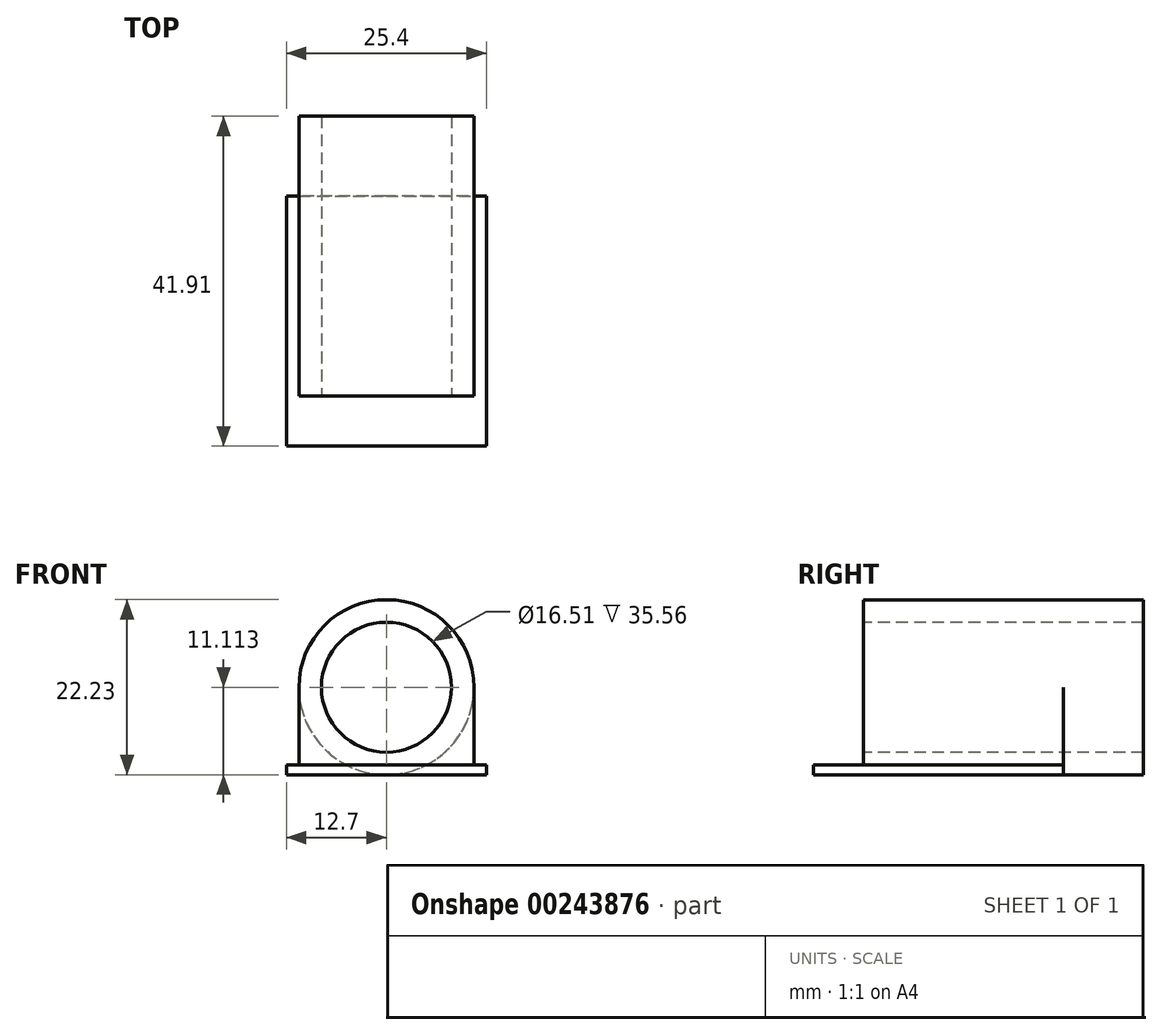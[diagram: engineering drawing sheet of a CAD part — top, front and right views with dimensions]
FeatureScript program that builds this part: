
annotation { "Feature Type Name" : "Feature", "Feature Type Description" : "" }
export const myFeature = defineFeature(function(context is Context, id is Id, definition is map)
    precondition{}
    {
        {
            var Q0;
            Q0=qCreatedBy(makeId("Top.planeOp"),FACE);
            var sketch = newSketch(context, id + "F0", { "sketchPlane" : qUnion([Q0])});
            skCircle(sketch, "E0", {"center": v(0, 0) * mm, "radius": 11.11 * mm});
            skSolve(sketch);
        }
        {
            var Q0;
            Q0=qSketchRegion(id+"F0",true);
            extrude(context, id + "F1", {"entities" : qUnion([Q0]), "depth" : 10.16 * mm, "hasSecondDirection" : true, "secondDirectionOppositeDirection" : true, "secondDirectionDepth" : 25.4 * mm});
        }
        {
            var Q0;
            Q0=makeQuery(id+"F1.opExtrude","CAP_FACE",FACE,{"disambiguationData":[OSD([sQuery(id+"F0.wireOp",EDGE,"E0")])],"isStart":false});
            var sketch = newSketch(context, id + "F2", { "sketchPlane" : qUnion([Q0])});
            skLineSegment(sketch, "E1.bottom", {"start": v(12.7, -11.11) * mm, "end": v(-12.7, -11.11) * mm});
            skLineSegment(sketch, "E1.top", {"start": v(12.7, -9.84) * mm, "end": v(-12.7, -9.84) * mm});
            skLineSegment(sketch, "E1.left", {"start": v(12.7, -11.11) * mm, "end": v(12.7, -9.84) * mm});
            skLineSegment(sketch, "E1.right", {"start": v(-12.7, -11.11) * mm, "end": v(-12.7, -9.84) * mm});
            skPoint(sketch, "E1.middle", {"position": v(0, -10.48) * mm});
            skSolve(sketch);
        }
        {
            var Q0;
            Q0=qSketchRegion(id+"F2",true);
            extrude(context, id + "F3", {"entities" : qUnion([Q0]), "operationType" : NewBodyOperationType.ADD, "depth" : 6.35 * mm, "hasSecondDirection" : true, "secondDirectionOppositeDirection" : true, "secondDirectionDepth" : 25.4 * mm});
        }
        {
            var Q0;
            Q0=qCreatedBy(makeId("Top.planeOp"),FACE);
            cPlane(context, id + "F4", {"entities" : qUnion([Q0]), "cplaneType" : CPlaneType.OFFSET, "offset" : 10.16 * mm, "width" : 152.4 * mm, "height" : 152.4 * mm});
        }
        {
            var Q0;
            Q0=qCreatedBy(id+"F4.planeOp",FACE);
            var sketch = newSketch(context, id + "F5", { "sketchPlane" : qUnion([Q0])});
            skArc(sketch, "E2", {"start": v(11.11, 0) * mm, "mid": v(0, 11.11) * mm, "end": v(-11.11, 0) * mm});
            skLineSegment(sketch, "E3", {"start": v(-11.11, 0) * mm, "end": v(-11.11, -10.67) * mm});
            skLineSegment(sketch, "E4", {"start": v(11.11, 0) * mm, "end": v(11.11, -10.67) * mm});
            skLineSegment(sketch, "E5", {"start": v(-11.11, -10.67) * mm, "end": v(11.11, -10.67) * mm});
            skSolve(sketch);
        }
        {
            var Q0;
            Q0=qSketchRegion(id+"F5",true);
            extrude(context, id + "F6", {"entities" : qUnion([Q0]), "operationType" : NewBodyOperationType.ADD, "oppositeDirection" : true, "depth" : 25.4 * mm});
        }
        {
            var Q0;
            Q0=makeQuery(id+"F1.opExtrude","CAP_FACE",FACE,{"disambiguationData":[OSD([sQuery(id+"F0.wireOp",EDGE,"E0")])],"isStart":false});
            var sketch = newSketch(context, id + "F7", { "sketchPlane" : qUnion([Q0])});
            skCircle(sketch, "E6", {"center": v(0, 0) * mm, "radius": 8.26 * mm});
            skSolve(sketch);
        }
        {
            var Q0;
            Q0=qSketchRegion(id+"F7",true);
            extrude(context, id + "F8", {"entities" : qUnion([Q0]), "operationType" : NewBodyOperationType.REMOVE, "endBound" : BoundingType.THROUGH_ALL, "oppositeDirection" : true, "depth" : 25.4 * mm});
        }
        {
            var Q0;
            Q0=makeQuery(id+"F1.opExtrude","SWEPT_BODY",BODY,{"disambiguationData":[OSD([sQuery(id+"F0.wireOp",EDGE,"E0")])]});
            var Q1;
            {var subQ0=sQuery(id+"F2.wireOp",EDGE,"E1.bottom");var subQ1=sQuery(id+"F2.wireOp",EDGE,"E1.right");Q1=makeQuery(id+"F3.boolean.opBoolean","SPLIT",EDGE,{"disambiguationData":[TD([makeQuery(id+"F3.opExtrude","SWEPT_FACE",FACE,{"disambiguationData":[OSD([subQ1])]})])],"derivedFrom":makeQuery(id+"F3.opExtrude","CAP_EDGE",EDGE,{"disambiguationData":[OSD([subQ0])],"isStart":true})});}
            transform(context, id + "F9", {"entities" : qUnion([Q0]), "transformType" : TransformType.ROTATION, "transformAxis" : qUnion([Q1]), "angle" : 270 * degree, "makeCopy" : false});
        }
    });
